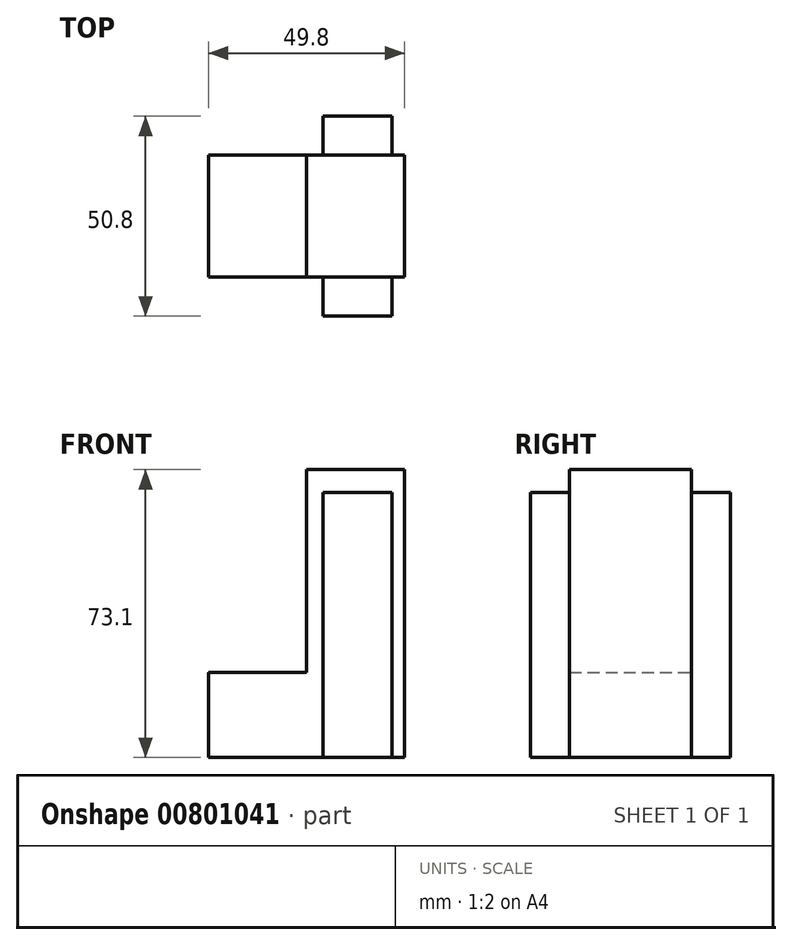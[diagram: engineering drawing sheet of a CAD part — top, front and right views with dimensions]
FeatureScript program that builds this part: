
annotation { "Feature Type Name" : "Feature", "Feature Type Description" : "" }
export const myFeature = defineFeature(function(context is Context, id is Id, definition is map)
    precondition{}
    {
        {
            var Q0;
            Q0=qCreatedBy(makeId("Front.planeOp"),FACE);
            var sketch = newSketch(context, id + "F0", { "sketchPlane" : qUnion([Q0])});
            skLineSegment(sketch, "E0.bottom", {"start": v(-24.9, 10.8) * mm, "end": v(24.9, 10.8) * mm});
            skLineSegment(sketch, "E0.top", {"start": v(-24.9, -10.8) * mm, "end": v(24.9, -10.8) * mm});
            skLineSegment(sketch, "E0.left", {"start": v(-24.9, 10.8) * mm, "end": v(-24.9, -10.8) * mm});
            skLineSegment(sketch, "E0.right", {"start": v(24.9, 10.8) * mm, "end": v(24.9, -10.8) * mm});
            skPoint(sketch, "E0.middle", {"position": v(0, 0) * mm});
            skLineSegment(sketch, "E1.bottom", {"start": v(24.9, 10.8) * mm, "end": v(0, 10.8) * mm});
            skLineSegment(sketch, "E1.top", {"start": v(24.9, 62.3) * mm, "end": v(0, 62.3) * mm});
            skLineSegment(sketch, "E1.left", {"start": v(24.9, 10.8) * mm, "end": v(24.9, 62.3) * mm});
            skLineSegment(sketch, "E1.right", {"start": v(0, 10.8) * mm, "end": v(0, 62.3) * mm});
            skLineSegment(sketch, "E2.bottom", {"start": v(4.17, 56.55) * mm, "end": v(21.73, 56.55) * mm});
            skLineSegment(sketch, "E2.top", {"start": v(4.17, -10.8) * mm, "end": v(21.73, -10.8) * mm});
            skLineSegment(sketch, "E2.left", {"start": v(4.17, 56.55) * mm, "end": v(4.17, -10.8) * mm});
            skLineSegment(sketch, "E2.right", {"start": v(21.73, 56.55) * mm, "end": v(21.73, -10.8) * mm});
            skLineSegment(sketch, "E3", {"start": v(4.17, -10.8) * mm, "end": v(4.17, 56.55) * mm});
            skSolve(sketch);
        }
        {
            var Q0;
            {var subQ0=sQuery(id+"F0.wireOp",EDGE,"E0.left");Q0=makeQuery(id+"F0.imprint","IMPRINT",FACE,{"disambiguationData":[TD([[makeQuery(id+"F0.imprint","IMPRINT",EDGE,{"derivedFrom":subQ0}),1.0]])]});}
            var Q1;
            {var subQ0=sQuery(id+"F0.wireOp",EDGE,"E0.right");Q1=makeQuery(id+"F0.imprint","IMPRINT",FACE,{"disambiguationData":[TD([[makeQuery(id+"F0.imprint","IMPRINT",EDGE,{"derivedFrom":subQ0}),-1.0]])]});}
            var Q2;
            Q2=makeQuery(id+"F0.imprint","IMPRINT",FACE,{"disambiguationData":[TD([[makeQuery(id+"F0.imprint","IMPRINT",EDGE,{"derivedFrom":sQuery(id+"F0.wireOp",EDGE,"E1.top")}),1.0]])]});
            extrude(context, id + "F1", {"entities" : qUnion([Q0, Q1, Q2]), "depth" : 15.5 * mm, "offsetDistance" : 25.4 * mm});
        }
        {
            var Q0;
            {var subQ5=sQuery(id+"F0.wireOp",EDGE,"E2.bottom");Q0=makeQuery(id+"F0.imprint","IMPRINT",FACE,{"disambiguationData":[TD([[makeQuery(id+"F0.imprint","IMPRINT",EDGE,{"derivedFrom":subQ5}),-1.0]])]});}
            extrude(context, id + "F2", {"entities" : qUnion([Q0]), "operationType" : NewBodyOperationType.ADD, "depth" : 25.4 * mm, "offsetDistance" : 25.4 * mm});
        }
        {
            var Q0;
            {var subQ0=sQuery(id+"F0.wireOp",EDGE,"E2.left");var subQ1=sQuery(id+"F0.wireOp",EDGE,"E0.bottom");var subQ2=makeQuery(id+"F0.imprint","INTERSECT",VERTEX,{"derivedFrom":[subQ1,subQ0]});Q0=makeQuery(id+"F0.imprint","IMPRINT",FACE,{"disambiguationData":[TD([[makeQuery(id+"F0.imprint","IMPRINT",EDGE,{"disambiguationData":[TD([[subQ2,-1.0]])],"derivedFrom":subQ1}),-1.0]])]});}
            extrude(context, id + "F3", {"entities" : qUnion([Q0]), "operationType" : NewBodyOperationType.ADD, "depth" : 25.4 * mm, "offsetDistance" : 25.4 * mm});
        }
        {
            var Q0;
            Q0=makeQuery(id+"F1.opExtrude","SWEPT_BODY",BODY,{"disambiguationData":[OSD([sQuery(id+"F0.wireOp",EDGE,"E0.bottom"),sQuery(id+"F0.wireOp",EDGE,"E0.top"),sQuery(id+"F0.wireOp",EDGE,"E0.left"),sQuery(id+"F0.wireOp",EDGE,"E0.right"),sQuery(id+"F0.wireOp",EDGE,"E1.top"),sQuery(id+"F0.wireOp",EDGE,"E1.left"),sQuery(id+"F0.wireOp",EDGE,"E1.right"),sQuery(id+"F0.wireOp",EDGE,"E2.bottom"),sQuery(id+"F0.wireOp",EDGE,"E2.left"),sQuery(id+"F0.wireOp",EDGE,"E2.right")])]});
            var Q1;
            Q1=qCreatedBy(makeId("Front.planeOp"),FACE);
            mirror(context, id + "F4", {"operationType" : NewBodyOperationType.ADD, "entities" : qUnion([Q0]), "mirrorPlane" : qUnion([Q1])});
        }
    });
